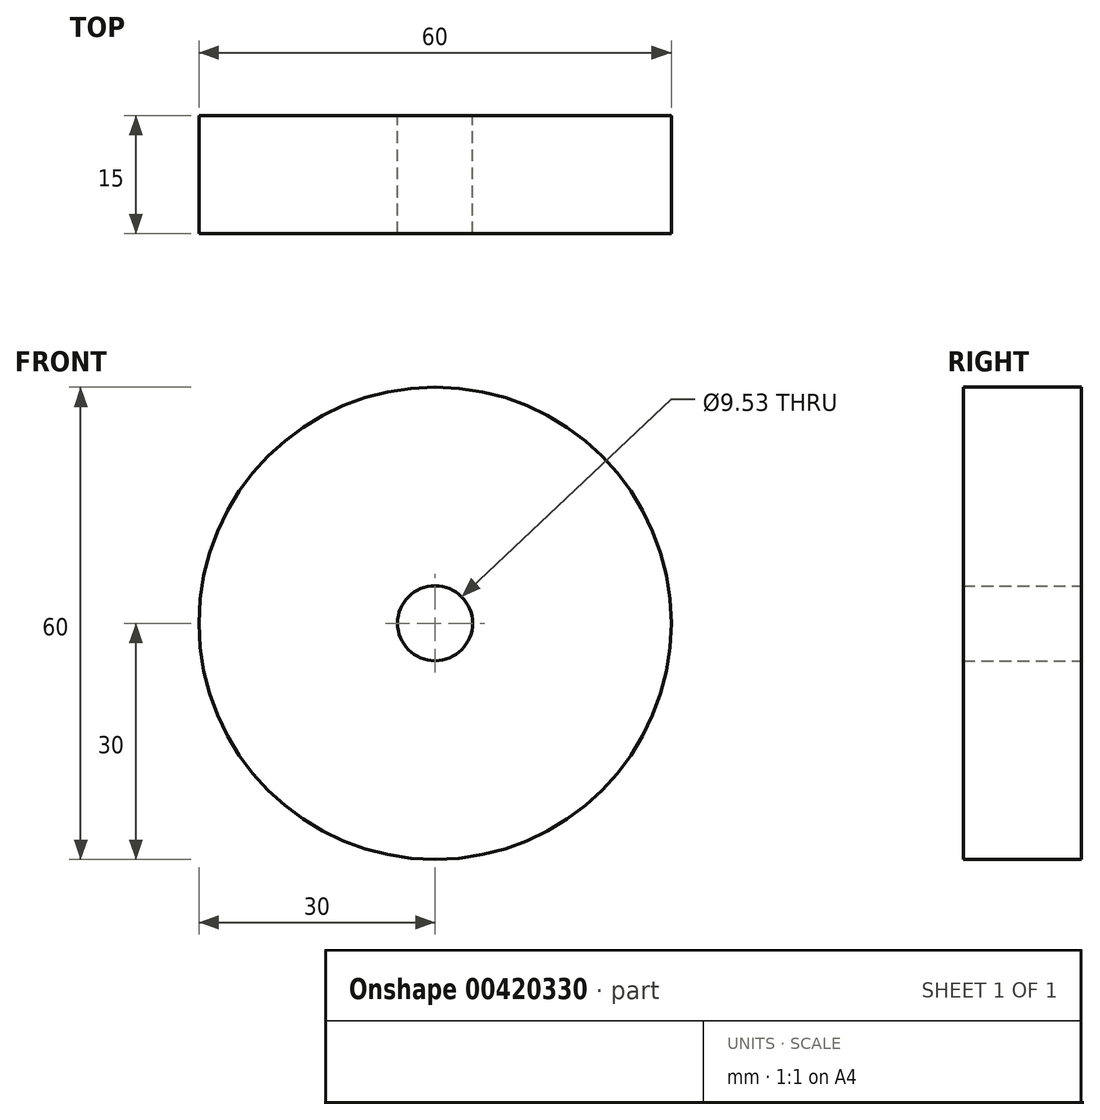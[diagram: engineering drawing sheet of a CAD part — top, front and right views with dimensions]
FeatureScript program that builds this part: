
annotation { "Feature Type Name" : "Feature", "Feature Type Description" : "" }
export const myFeature = defineFeature(function(context is Context, id is Id, definition is map)
    precondition{}
    {
        {
            var Q0;
            Q0=qCreatedBy(makeId("Front.planeOp"),FACE);
            var sketch = newSketch(context, id + "F0", { "sketchPlane" : qUnion([Q0])});
            skCircle(sketch, "E0", {"center": v(0, 0) * mm, "radius": 30 * mm});
            skCircle(sketch, "E1", {"center": v(0, 0) * mm, "radius": 4.76 * mm});
            skSolve(sketch);
        }
        {
            var Q0;
            Q0=qSketchRegion(id+"F0",true);
            extrude(context, id + "F1", {"entities" : qUnion([Q0]), "depth" : 15 * mm});
        }
    });
